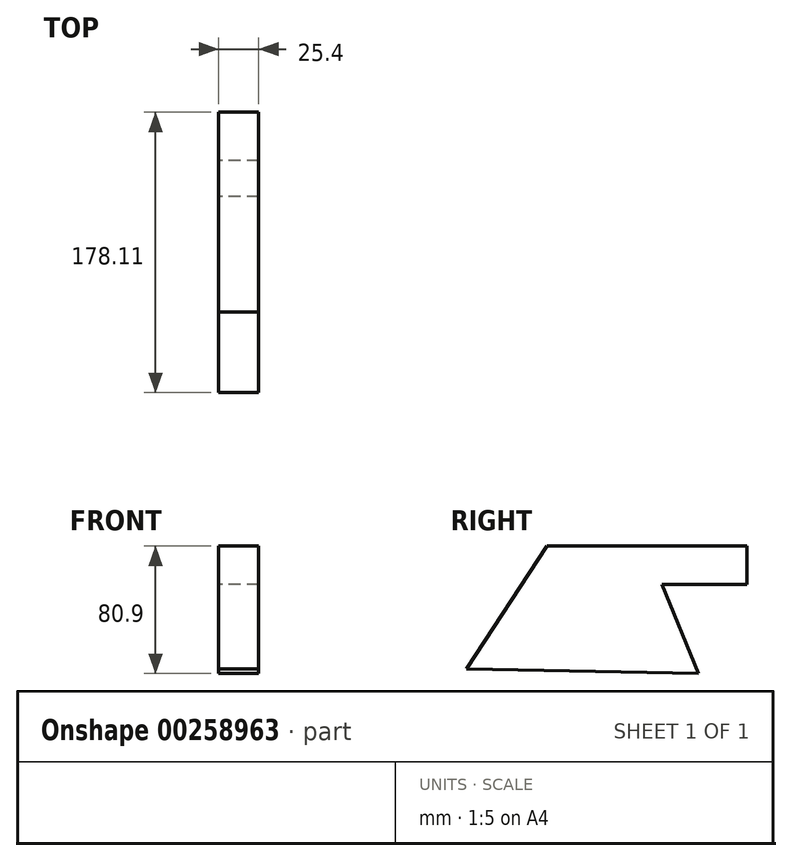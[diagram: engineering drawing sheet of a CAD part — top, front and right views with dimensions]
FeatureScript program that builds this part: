
annotation { "Feature Type Name" : "Feature", "Feature Type Description" : "" }
export const myFeature = defineFeature(function(context is Context, id is Id, definition is map)
    precondition{}
    {
        {
            var Q0;
            Q0=qCreatedBy(makeId("Right.planeOp"),FACE);
            var sketch = newSketch(context, id + "F0", { "sketchPlane" : qUnion([Q0])});
            skLineSegment(sketch, "E0", {"start": v(-69.96, -68.92) * mm, "end": v(-18.83, 8.96) * mm});
            skLineSegment(sketch, "E1", {"start": v(-18.83, 8.96) * mm, "end": v(44.52, 8.96) * mm});
            skLineSegment(sketch, "E2", {"start": v(44.52, 8.96) * mm, "end": v(77.34, -71.94) * mm});
            skLineSegment(sketch, "E3", {"start": v(77.34, -71.94) * mm, "end": v(-69.96, -68.92) * mm});
            skLineSegment(sketch, "E4", {"start": v(108.15, 8.96) * mm, "end": v(44.52, 8.96) * mm});
            skLineSegment(sketch, "E5", {"start": v(108.15, -15.36) * mm, "end": v(108.15, 8.96) * mm});
            skLineSegment(sketch, "E6", {"start": v(54.39, -15.36) * mm, "end": v(108.15, -15.36) * mm});
            skSolve(sketch);
        }
        {
            var Q0;
            Q0 = qSketchRegion(id + "F0", true);
            extrude(context, id + "F1", {"entities" : qUnion([Q0]), "depth" : 25.4 * mm});
        }
    });
